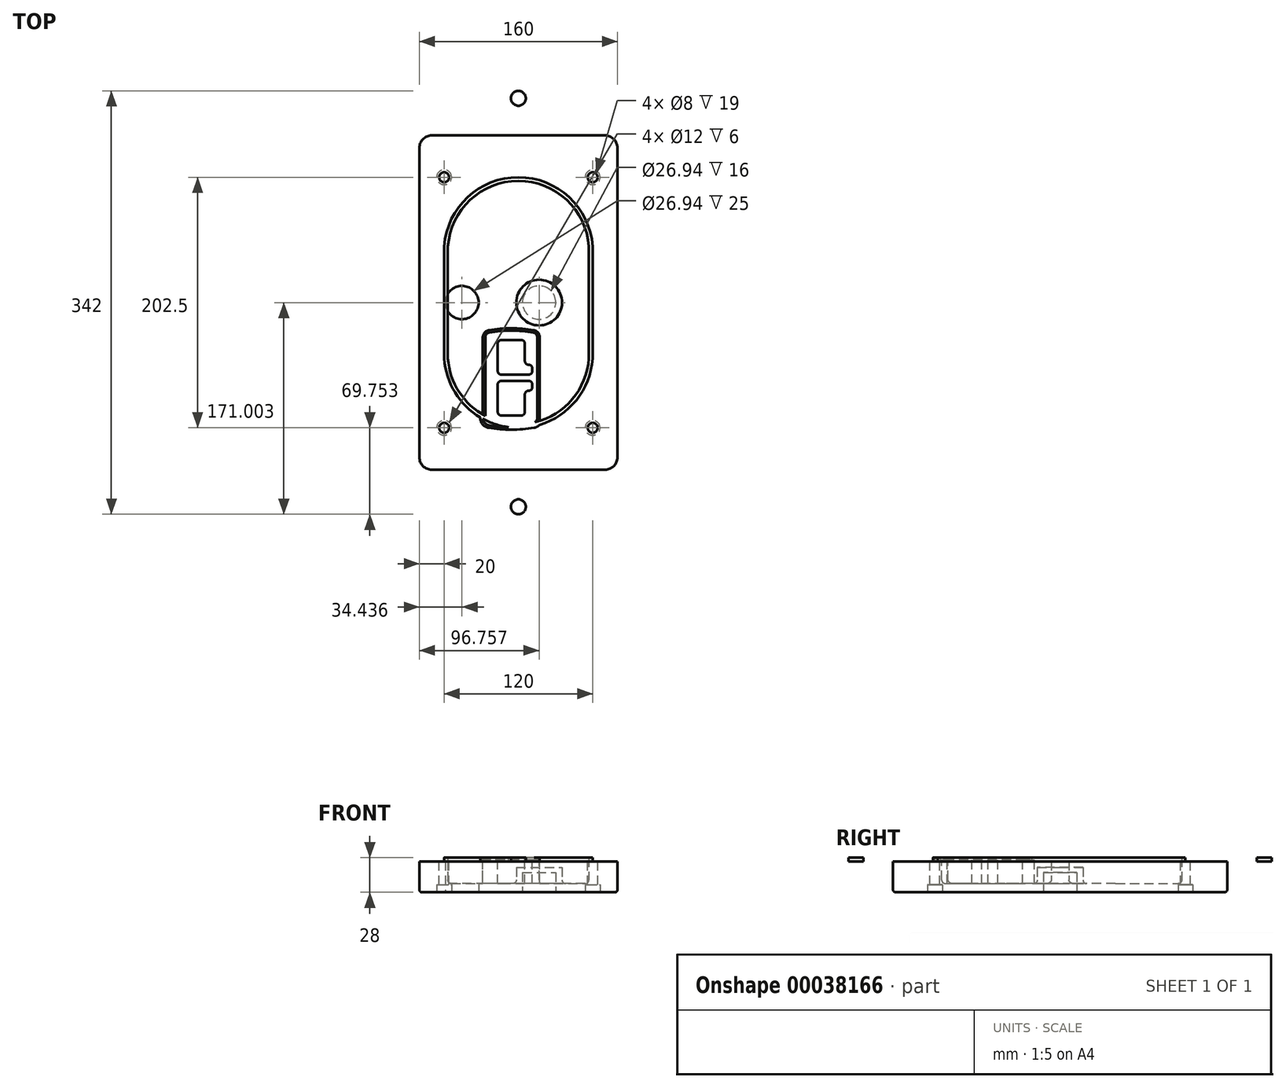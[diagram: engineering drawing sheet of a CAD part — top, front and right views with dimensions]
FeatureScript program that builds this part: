
annotation { "Feature Type Name" : "Feature", "Feature Type Description" : "" }
export const myFeature = defineFeature(function(context is Context, id is Id, definition is map)
    precondition{}
    {
        {
            var Q0;
            Q0=qCreatedBy(makeId("Top.planeOp"),FACE);
            var sketch = newSketch(context, id + "F0", { "sketchPlane" : qUnion([Q0])});
            skPoint(sketch, "E0.rect.middle", {"position": v(0, 0) * mm});
            skLineSegment(sketch, "E1.bottom", {"start": v(24.05, 28.38) * mm, "end": v(164.05, 28.38) * mm});
            skLineSegment(sketch, "E1.top", {"start": v(24.05, 298.38) * mm, "end": v(164.05, 298.38) * mm});
            skLineSegment(sketch, "E1.left", {"start": v(14.05, 38.38) * mm, "end": v(14.05, 288.38) * mm});
            skLineSegment(sketch, "E1.right", {"start": v(174.05, 38.38) * mm, "end": v(174.05, 288.38) * mm});
            skLineSegment(sketch, "E2", {"start": v(14.05, 298.38) * mm, "end": v(174.05, 28.38) * mm, "construction": true});
            skLineSegment(sketch, "E3", {"start": v(174.05, 298.38) * mm, "end": v(14.05, 28.38) * mm, "construction": true});
            skCircle(sketch, "E4", {"center": v(34.05, 264.63) * mm, "radius": 4 * mm});
            skCircle(sketch, "E5", {"center": v(154.05, 264.63) * mm, "radius": 4 * mm});
            skCircle(sketch, "E6", {"center": v(154.05, 62.13) * mm, "radius": 4 * mm});
            skCircle(sketch, "E7", {"center": v(34.05, 62.13) * mm, "radius": 4 * mm});
            skLineSegment(sketch, "E8", {"start": v(34.05, 264.63) * mm, "end": v(154.05, 264.63) * mm, "construction": true});
            skLineSegment(sketch, "E9", {"start": v(154.05, 264.63) * mm, "end": v(154.05, 62.13) * mm, "construction": true});
            skLineSegment(sketch, "E10", {"start": v(154.05, 62.13) * mm, "end": v(34.05, 62.13) * mm, "construction": true});
            skLineSegment(sketch, "E11", {"start": v(34.05, 62.13) * mm, "end": v(34.05, 264.63) * mm, "construction": true});
            skLineSegment(sketch, "E12", {"start": v(34.05, 208.05) * mm, "end": v(34.05, 118.72) * mm});
            skLineSegment(sketch, "E13", {"start": v(154.05, 208.05) * mm, "end": v(154.05, 118.72) * mm});
            skArc(sketch, "E14", {"start": v(154.03, 208.75) * mm, "mid": v(94.05, 264.63) * mm, "end": v(34.07, 208.75) * mm});
            skArc(sketch, "E15", {"start": v(34.07, 118.01) * mm, "mid": v(94.05, 62.13) * mm, "end": v(154.03, 118.01) * mm});
            skLineSegment(sketch, "E16", {"start": v(34.05, 163.38) * mm, "end": v(154.05, 163.38) * mm, "construction": true});
            skPoint(sketch, "E17.visualSharp", {"position": v(34.05, 118.38) * mm});
            skArc(sketch, "E17.filletArc", {"start": v(34.05, 118.72) * mm, "mid": v(34.06, 118.37) * mm, "end": v(34.07, 118.01) * mm});
            skPoint(sketch, "E18.visualSharp", {"position": v(34.05, 208.38) * mm});
            skArc(sketch, "E18.filletArc", {"start": v(34.07, 208.75) * mm, "mid": v(34.06, 208.4) * mm, "end": v(34.05, 208.05) * mm});
            skPoint(sketch, "E19.visualSharp", {"position": v(154.05, 208.38) * mm});
            skArc(sketch, "E19.filletArc", {"start": v(154.05, 208.05) * mm, "mid": v(154.04, 208.4) * mm, "end": v(154.03, 208.75) * mm});
            skPoint(sketch, "E20.visualSharp", {"position": v(154.05, 118.38) * mm});
            skArc(sketch, "E20.filletArc", {"start": v(154.03, 118.01) * mm, "mid": v(154.04, 118.37) * mm, "end": v(154.05, 118.72) * mm});
            skPoint(sketch, "E21.visualSharp", {"position": v(14.05, 298.38) * mm});
            skArc(sketch, "E21.filletArc", {"start": v(24.05, 298.38) * mm, "mid": v(16.98, 295.45) * mm, "end": v(14.05, 288.38) * mm});
            skPoint(sketch, "E22.visualSharp", {"position": v(174.05, 298.38) * mm});
            skArc(sketch, "E22.filletArc", {"start": v(174.05, 288.38) * mm, "mid": v(171.12, 295.45) * mm, "end": v(164.05, 298.38) * mm});
            skPoint(sketch, "E23.visualSharp", {"position": v(174.05, 28.38) * mm});
            skArc(sketch, "E23.filletArc", {"start": v(164.05, 28.38) * mm, "mid": v(171.12, 31.31) * mm, "end": v(174.05, 38.38) * mm});
            skPoint(sketch, "E24.visualSharp", {"position": v(14.05, 28.38) * mm});
            skArc(sketch, "E24.filletArc", {"start": v(14.05, 38.38) * mm, "mid": v(16.98, 31.31) * mm, "end": v(24.05, 28.38) * mm});
            skArc(sketch, "E25.0", {"start": v(151.05, 208.05) * mm, "mid": v(151.05, 208.3) * mm, "end": v(151.03, 208.54) * mm});
            skLineSegment(sketch, "E25.1", {"start": v(151.05, 208.05) * mm, "end": v(151.05, 118.72) * mm});
            skArc(sketch, "E25.2", {"start": v(151.03, 118.23) * mm, "mid": v(151.05, 118.47) * mm, "end": v(151.05, 118.72) * mm});
            skArc(sketch, "E25.3", {"start": v(37.07, 118.23) * mm, "mid": v(94.05, 65.13) * mm, "end": v(151.03, 118.23) * mm});
            skArc(sketch, "E25.4", {"start": v(37.05, 118.72) * mm, "mid": v(37.05, 118.47) * mm, "end": v(37.07, 118.23) * mm});
            skArc(sketch, "E25.5", {"start": v(151.03, 208.54) * mm, "mid": v(94.05, 261.63) * mm, "end": v(37.07, 208.54) * mm});
            skLineSegment(sketch, "E25.6", {"start": v(37.05, 208.05) * mm, "end": v(37.05, 118.72) * mm});
            skArc(sketch, "E25.7", {"start": v(37.07, 208.54) * mm, "mid": v(37.05, 208.3) * mm, "end": v(37.05, 208.05) * mm});
            skArc(sketch, "E26.0", {"start": v(30.08, 209.03) * mm, "mid": v(30.06, 208.54) * mm, "end": v(30.05, 208.05) * mm});
            skArc(sketch, "E26.1", {"start": v(158.02, 209.03) * mm, "mid": v(94.05, 268.63) * mm, "end": v(30.08, 209.03) * mm});
            skArc(sketch, "E26.2", {"start": v(158.05, 208.05) * mm, "mid": v(158.04, 208.54) * mm, "end": v(158.02, 209.03) * mm});
            skLineSegment(sketch, "E26.3", {"start": v(158.05, 208.05) * mm, "end": v(158.05, 118.72) * mm});
            skArc(sketch, "E26.4", {"start": v(158.02, 117.73) * mm, "mid": v(158.04, 118.23) * mm, "end": v(158.05, 118.72) * mm});
            skLineSegment(sketch, "E26.5", {"start": v(30.05, 208.05) * mm, "end": v(30.05, 118.72) * mm});
            skArc(sketch, "E26.6", {"start": v(30.08, 117.73) * mm, "mid": v(94.05, 58.13) * mm, "end": v(158.02, 117.73) * mm});
            skArc(sketch, "E26.7", {"start": v(30.05, 118.72) * mm, "mid": v(30.06, 118.23) * mm, "end": v(30.08, 117.73) * mm});
            skSolve(sketch);
        }
        {
            var Q0;
            Q0=makeQuery(id+"F0.imprint","IMPRINT",FACE,{"disambiguationData":[TD([[makeQuery(id+"F0.imprint","IMPRINT",EDGE,{"derivedFrom":sQuery(id+"F0.wireOp",EDGE,"E1.bottom")}),1.0]])]});
            var Q1;
            Q1=makeQuery(id+"F0.imprint","IMPRINT",FACE,{"disambiguationData":[TD([[makeQuery(id+"F0.imprint","IMPRINT",EDGE,{"derivedFrom":sQuery(id+"F0.wireOp",EDGE,"E12")}),1.0]])]});
            var Q2;
            Q2=makeQuery(id+"F0.imprint","IMPRINT",FACE,{"disambiguationData":[TD([[makeQuery(id+"F0.imprint","IMPRINT",EDGE,{"derivedFrom":sQuery(id+"F0.wireOp",EDGE,"E25.0")}),1.0]])]});
            var Q3;
            Q3=makeQuery(id+"F0.imprint","IMPRINT",FACE,{"disambiguationData":[TD([[makeQuery(id+"F0.imprint","IMPRINT",EDGE,{"derivedFrom":sQuery(id+"F0.wireOp",EDGE,"E12")}),-1.0]])]});
            extrude(context, id + "F1", {"entities" : qUnion([Q0, Q1, Q2, Q3]), "oppositeDirection" : true, "depth" : 25 * mm});
        }
        {
            var Q0;
            Q0=makeQuery(id+"F0.imprint","IMPRINT",FACE,{"disambiguationData":[TD([[makeQuery(id+"F0.imprint","IMPRINT",EDGE,{"derivedFrom":sQuery(id+"F0.wireOp",EDGE,"E12")}),1.0]])]});
            extrude(context, id + "F2", {"entities" : qUnion([Q0]), "operationType" : NewBodyOperationType.ADD, "depth" : 3 * mm});
        }
        {
            var Q0;
            Q0=makeQuery(id+"F0.imprint","IMPRINT",FACE,{"disambiguationData":[TD([[makeQuery(id+"F0.imprint","IMPRINT",EDGE,{"derivedFrom":sQuery(id+"F0.wireOp",EDGE,"E25.0")}),1.0]])]});
            extrude(context, id + "F3", {"entities" : qUnion([Q0]), "operationType" : NewBodyOperationType.REMOVE, "oppositeDirection" : true, "depth" : 18 * mm});
        }
        {
            var Q0;
            Q0=makeQuery(id+"F2.opExtrude","CAP_FACE",FACE,{"disambiguationData":[OSD([sQuery(id+"F0.wireOp",EDGE,"E12"),sQuery(id+"F0.wireOp",EDGE,"E13"),sQuery(id+"F0.wireOp",EDGE,"E14"),sQuery(id+"F0.wireOp",EDGE,"E15"),sQuery(id+"F0.wireOp",EDGE,"E17.filletArc"),sQuery(id+"F0.wireOp",EDGE,"E18.filletArc"),sQuery(id+"F0.wireOp",EDGE,"E19.filletArc"),sQuery(id+"F0.wireOp",EDGE,"E20.filletArc"),sQuery(id+"F0.wireOp",EDGE,"E25.0"),sQuery(id+"F0.wireOp",EDGE,"E25.1"),sQuery(id+"F0.wireOp",EDGE,"E25.2"),sQuery(id+"F0.wireOp",EDGE,"E25.3"),sQuery(id+"F0.wireOp",EDGE,"E25.4"),sQuery(id+"F0.wireOp",EDGE,"E25.5"),sQuery(id+"F0.wireOp",EDGE,"E25.6"),sQuery(id+"F0.wireOp",EDGE,"E25.7")])],"isStart":false});
            var sketch = newSketch(context, id + "F4", { "sketchPlane" : qUnion([Q0])});
            skArc(sketch, "E27.0", {"start": v(69.96, 62.18) * mm, "mid": v(88.3, 60.63) * mm, "end": v(106.64, 62.18) * mm});
            skArc(sketch, "E28.0", {"start": v(106.64, 143.09) * mm, "mid": v(88.3, 144.63) * mm, "end": v(69.96, 143.09) * mm});
            skLineSegment(sketch, "E29", {"start": v(63.3, 135.2) * mm, "end": v(63.3, 70.07) * mm});
            skLineSegment(sketch, "E30", {"start": v(113.3, 135.2) * mm, "end": v(113.3, 70.07) * mm});
            skLineSegment(sketch, "E31", {"start": v(63.3, 141.74) * mm, "end": v(113.3, 141.74) * mm, "construction": true});
            skLineSegment(sketch, "E32", {"start": v(63.3, 63.52) * mm, "end": v(113.3, 63.52) * mm, "construction": true});
            skPoint(sketch, "E33.visualSharp", {"position": v(63.3, 141.74) * mm});
            skArc(sketch, "E33.filletArc", {"start": v(69.96, 143.09) * mm, "mid": v(65.19, 140.36) * mm, "end": v(63.3, 135.2) * mm});
            skPoint(sketch, "E34.visualSharp", {"position": v(113.3, 141.74) * mm});
            skArc(sketch, "E34.filletArc", {"start": v(113.3, 135.2) * mm, "mid": v(111.41, 140.36) * mm, "end": v(106.64, 143.09) * mm});
            skPoint(sketch, "E35.visualSharp", {"position": v(113.3, 63.52) * mm});
            skArc(sketch, "E35.filletArc", {"start": v(106.64, 62.18) * mm, "mid": v(111.41, 64.9) * mm, "end": v(113.3, 70.07) * mm});
            skPoint(sketch, "E36.visualSharp", {"position": v(63.3, 63.52) * mm});
            skArc(sketch, "E36.filletArc", {"start": v(63.3, 70.07) * mm, "mid": v(65.19, 64.9) * mm, "end": v(69.96, 62.18) * mm});
            skArc(sketch, "E37.0", {"start": v(151.03, 208.54) * mm, "mid": v(94.05, 261.63) * mm, "end": v(37.07, 208.54) * mm});
            skArc(sketch, "E37.1", {"start": v(37.07, 208.54) * mm, "mid": v(37.05, 208.3) * mm, "end": v(37.05, 208.05) * mm});
            skLineSegment(sketch, "E37.2", {"start": v(37.05, 208.05) * mm, "end": v(37.05, 118.72) * mm});
            skArc(sketch, "E37.3", {"start": v(37.05, 118.72) * mm, "mid": v(37.05, 118.47) * mm, "end": v(37.07, 118.23) * mm});
            skArc(sketch, "E37.4", {"start": v(37.07, 118.23) * mm, "mid": v(94.05, 65.13) * mm, "end": v(151.03, 118.23) * mm});
            skArc(sketch, "E37.5", {"start": v(151.03, 118.23) * mm, "mid": v(151.05, 118.47) * mm, "end": v(151.05, 118.72) * mm});
            skLineSegment(sketch, "E37.6", {"start": v(151.05, 208.05) * mm, "end": v(151.05, 118.72) * mm});
            skArc(sketch, "E37.7", {"start": v(151.05, 208.05) * mm, "mid": v(151.05, 208.3) * mm, "end": v(151.03, 208.54) * mm});
            skLineSegment(sketch, "E38.0", {"start": v(111.3, 135.2) * mm, "end": v(111.3, 70.07) * mm});
            skArc(sketch, "E38.1", {"start": v(106.3, 64.15) * mm, "mid": v(109.88, 66.2) * mm, "end": v(111.3, 70.07) * mm});
            skArc(sketch, "E38.2", {"start": v(70.3, 64.15) * mm, "mid": v(88.3, 62.63) * mm, "end": v(106.3, 64.15) * mm});
            skArc(sketch, "E38.3", {"start": v(65.3, 70.07) * mm, "mid": v(66.72, 66.2) * mm, "end": v(70.3, 64.15) * mm});
            skLineSegment(sketch, "E38.4", {"start": v(65.3, 135.2) * mm, "end": v(65.3, 70.07) * mm});
            skArc(sketch, "E38.5", {"start": v(111.3, 135.2) * mm, "mid": v(109.88, 139.07) * mm, "end": v(106.3, 141.11) * mm});
            skArc(sketch, "E38.6", {"start": v(70.3, 141.11) * mm, "mid": v(66.72, 139.07) * mm, "end": v(65.3, 135.2) * mm});
            skArc(sketch, "E38.7", {"start": v(106.3, 141.11) * mm, "mid": v(88.3, 142.63) * mm, "end": v(70.3, 141.11) * mm});
            skArc(sketch, "E39.0", {"start": v(109.3, 135.2) * mm, "mid": v(108.36, 137.78) * mm, "end": v(105.97, 139.14) * mm});
            skLineSegment(sketch, "E39.1", {"start": v(109.3, 135.2) * mm, "end": v(109.3, 70.07) * mm});
            skArc(sketch, "E39.2", {"start": v(105.97, 66.12) * mm, "mid": v(108.36, 67.49) * mm, "end": v(109.3, 70.07) * mm});
            skArc(sketch, "E39.3", {"start": v(70.63, 66.12) * mm, "mid": v(88.3, 64.63) * mm, "end": v(105.97, 66.12) * mm});
            skArc(sketch, "E39.4", {"start": v(67.3, 70.07) * mm, "mid": v(68.24, 67.49) * mm, "end": v(70.63, 66.12) * mm});
            skArc(sketch, "E39.5", {"start": v(105.97, 139.14) * mm, "mid": v(88.3, 140.63) * mm, "end": v(70.63, 139.14) * mm});
            skLineSegment(sketch, "E39.6", {"start": v(67.3, 135.2) * mm, "end": v(67.3, 70.07) * mm});
            skArc(sketch, "E39.7", {"start": v(70.63, 139.14) * mm, "mid": v(68.24, 137.78) * mm, "end": v(67.3, 135.2) * mm});
            skLineSegment(sketch, "E40", {"start": v(63.3, 102.63) * mm, "end": v(113.3, 102.63) * mm, "construction": true});
            skLineSegment(sketch, "E41", {"start": v(77.3, 108.13) * mm, "end": v(77.3, 130.13) * mm});
            skLineSegment(sketch, "E42", {"start": v(80.3, 133.13) * mm, "end": v(96.3, 133.13) * mm});
            skLineSegment(sketch, "E43", {"start": v(99.3, 130.13) * mm, "end": v(99.3, 116.13) * mm});
            skLineSegment(sketch, "E44", {"start": v(102.3, 113.13) * mm, "end": v(102.3, 113.13) * mm});
            skLineSegment(sketch, "E45", {"start": v(105.3, 110.13) * mm, "end": v(105.3, 108.13) * mm});
            skLineSegment(sketch, "E46", {"start": v(102.3, 105.13) * mm, "end": v(80.3, 105.13) * mm});
            skPoint(sketch, "E47.visualSharp", {"position": v(77.3, 133.13) * mm});
            skArc(sketch, "E47.filletArc", {"start": v(80.3, 133.13) * mm, "mid": v(78.18, 132.25) * mm, "end": v(77.3, 130.13) * mm});
            skPoint(sketch, "E48.visualSharp", {"position": v(99.3, 133.13) * mm});
            skArc(sketch, "E48.filletArc", {"start": v(99.3, 130.13) * mm, "mid": v(98.42, 132.25) * mm, "end": v(96.3, 133.13) * mm});
            skPoint(sketch, "E49.visualSharp", {"position": v(99.3, 113.13) * mm});
            skArc(sketch, "E49.filletArc", {"start": v(99.3, 116.13) * mm, "mid": v(100.18, 114.01) * mm, "end": v(102.3, 113.13) * mm});
            skPoint(sketch, "E50.visualSharp", {"position": v(105.3, 113.13) * mm});
            skArc(sketch, "E50.filletArc", {"start": v(105.3, 110.13) * mm, "mid": v(104.42, 112.25) * mm, "end": v(102.3, 113.13) * mm});
            skPoint(sketch, "E51.visualSharp", {"position": v(105.3, 105.13) * mm});
            skArc(sketch, "E51.filletArc", {"start": v(102.3, 105.13) * mm, "mid": v(104.42, 106.01) * mm, "end": v(105.3, 108.13) * mm});
            skPoint(sketch, "E52.visualSharp", {"position": v(77.3, 105.13) * mm});
            skArc(sketch, "E52.filletArc", {"start": v(77.3, 108.13) * mm, "mid": v(78.18, 106.01) * mm, "end": v(80.3, 105.13) * mm});
            skLineSegment(sketch, "E53.0.MirrorCS", {"start": v(102.3, 100.13) * mm, "end": v(80.3, 100.13) * mm});
            skArc(sketch, "E54.0.MirrorCS", {"start": v(77.3, 97.13) * mm, "mid": v(78.18, 99.25) * mm, "end": v(80.3, 100.13) * mm});
            skLineSegment(sketch, "E55.0.MirrorCS", {"start": v(77.3, 97.13) * mm, "end": v(77.3, 75.13) * mm});
            skArc(sketch, "E56.0.MirrorCS", {"start": v(80.3, 72.13) * mm, "mid": v(78.18, 73.01) * mm, "end": v(77.3, 75.13) * mm});
            skLineSegment(sketch, "E57.0.MirrorCS", {"start": v(80.3, 72.13) * mm, "end": v(96.3, 72.13) * mm});
            skArc(sketch, "E58.0.MirrorCS", {"start": v(99.3, 75.13) * mm, "mid": v(98.42, 73.01) * mm, "end": v(96.3, 72.13) * mm});
            skLineSegment(sketch, "E59.0.MirrorCS", {"start": v(99.3, 75.13) * mm, "end": v(99.3, 89.13) * mm});
            skArc(sketch, "E60.0.MirrorCS", {"start": v(99.3, 89.13) * mm, "mid": v(100.18, 91.25) * mm, "end": v(102.3, 92.13) * mm});
            skArc(sketch, "E61.0.MirrorCS", {"start": v(105.3, 95.13) * mm, "mid": v(104.42, 93.01) * mm, "end": v(102.3, 92.13) * mm});
            skLineSegment(sketch, "E62.0.MirrorCS", {"start": v(105.3, 95.13) * mm, "end": v(105.3, 97.13) * mm});
            skArc(sketch, "E63.0.MirrorCS", {"start": v(102.3, 100.13) * mm, "mid": v(104.42, 99.25) * mm, "end": v(105.3, 97.13) * mm});
            skSolve(sketch);
        }
        {
            var Q0;
            Q0=makeQuery(id+"F4.imprint","IMPRINT",FACE,{"disambiguationData":[TD([[makeQuery(id+"F4.imprint","IMPRINT",EDGE,{"derivedFrom":sQuery(id+"F4.wireOp",EDGE,"E27.0")}),1.0]])]});
            var Q1;
            Q1=makeQuery(id+"F4.imprint","IMPRINT",FACE,{"disambiguationData":[TD([[makeQuery(id+"F4.imprint","IMPRINT",EDGE,{"derivedFrom":sQuery(id+"F4.wireOp",EDGE,"E38.0")}),-1.0]])]});
            var Q2;
            Q2=makeQuery(id+"F4.imprint","IMPRINT",FACE,{"disambiguationData":[TD([[makeQuery(id+"F4.imprint","IMPRINT",EDGE,{"derivedFrom":sQuery(id+"F4.wireOp",EDGE,"E39.0")}),1.0]])]});
            extrude(context, id + "F5", {"entities" : qUnion([Q0, Q1, Q2]), "operationType" : NewBodyOperationType.ADD, "endBound" : BoundingType.UP_TO_NEXT, "oppositeDirection" : true, "depth" : 25 * mm});
        }
        {
            var Q0;
            Q0=makeQuery(id+"F4.imprint","IMPRINT",FACE,{"disambiguationData":[TD([[makeQuery(id+"F4.imprint","IMPRINT",EDGE,{"derivedFrom":sQuery(id+"F4.wireOp",EDGE,"E38.0")}),-1.0]])]});
            extrude(context, id + "F6", {"entities" : qUnion([Q0]), "operationType" : NewBodyOperationType.REMOVE, "oppositeDirection" : true, "depth" : 2 * mm});
        }
        {
            var Q0;
            Q0=makeQuery(id+"F1.opExtrude","CAP_FACE",FACE,{"disambiguationData":[OSD([sQuery(id+"F0.wireOp",EDGE,"E1.bottom"),sQuery(id+"F0.wireOp",EDGE,"E1.top"),sQuery(id+"F0.wireOp",EDGE,"E1.left"),sQuery(id+"F0.wireOp",EDGE,"E1.right"),sQuery(id+"F0.wireOp",EDGE,"E4"),sQuery(id+"F0.wireOp",EDGE,"E5"),sQuery(id+"F0.wireOp",EDGE,"E6"),sQuery(id+"F0.wireOp",EDGE,"E7"),sQuery(id+"F0.wireOp",EDGE,"E21.filletArc"),sQuery(id+"F0.wireOp",EDGE,"E22.filletArc"),sQuery(id+"F0.wireOp",EDGE,"E23.filletArc"),sQuery(id+"F0.wireOp",EDGE,"E24.filletArc")])],"isStart":false});
            var sketch = newSketch(context, id + "F7", { "sketchPlane" : qUnion([Q0])});
            skCircle(sketch, "E64", {"center": v(110.8, -163.38) * mm, "radius": 13.47 * mm});
            skCircle(sketch, "E65", {"center": v(48.49, -163.38) * mm, "radius": 13.47 * mm});
            skLineSegment(sketch, "E66", {"start": v(174.05, -163.38) * mm, "end": v(14.05, -163.38) * mm});
            skCircle(sketch, "E67", {"center": v(110.8, -163.38) * mm, "radius": 18.47 * mm});
            skCircle(sketch, "E68", {"center": v(154.05, -264.63) * mm, "radius": 6 * mm});
            skCircle(sketch, "E69", {"center": v(34.05, -264.63) * mm, "radius": 6 * mm});
            skCircle(sketch, "E70", {"center": v(34.05, -62.13) * mm, "radius": 6 * mm});
            skCircle(sketch, "E71", {"center": v(154.05, -62.13) * mm, "radius": 6 * mm});
            skSolve(sketch);
        }
        {
            var Q0;
            {var subQ1=sQuery(id+"F7.wireOp",EDGE,"E66");var subQ4=sQuery(id+"F7.wireOp",EDGE,"E64");var subQ6=makeQuery(id+"F7.imprint","INTERSECT",VERTEX,{"disambiguationData":[OD(0.0)],"derivedFrom":[subQ4,subQ1]});Q0=makeQuery(id+"F7.imprint","IMPRINT",FACE,{"disambiguationData":[TD([[makeQuery(id+"F7.imprint","IMPRINT",EDGE,{"disambiguationData":[TD([[subQ6,-1.0]])],"derivedFrom":subQ4}),-1.0]])]});}
            var Q1;
            {var subQ0=sQuery(id+"F7.wireOp",EDGE,"E66");var subQ1=sQuery(id+"F7.wireOp",EDGE,"E64");var subQ3=makeQuery(id+"F7.imprint","INTERSECT",VERTEX,{"disambiguationData":[OD(0.0)],"derivedFrom":[subQ1,subQ0]});Q1=makeQuery(id+"F7.imprint","IMPRINT",FACE,{"disambiguationData":[TD([[makeQuery(id+"F7.imprint","IMPRINT",EDGE,{"disambiguationData":[TD([[subQ3,-1.0]])],"derivedFrom":subQ1}),1.0]])]});}
            var Q2;
            {var subQ0=sQuery(id+"F7.wireOp",EDGE,"E66");var subQ1=sQuery(id+"F7.wireOp",EDGE,"E64");var subQ3=makeQuery(id+"F7.imprint","INTERSECT",VERTEX,{"disambiguationData":[OD(0.0)],"derivedFrom":[subQ1,subQ0]});Q2=makeQuery(id+"F7.imprint","IMPRINT",FACE,{"disambiguationData":[TD([[makeQuery(id+"F7.imprint","IMPRINT",EDGE,{"disambiguationData":[TD([[subQ3,1.0]])],"derivedFrom":subQ1}),1.0]])]});}
            var Q3;
            {var subQ1=sQuery(id+"F7.wireOp",EDGE,"E66");var subQ4=sQuery(id+"F7.wireOp",EDGE,"E64");var subQ6=makeQuery(id+"F7.imprint","INTERSECT",VERTEX,{"disambiguationData":[OD(0.0)],"derivedFrom":[subQ4,subQ1]});Q3=makeQuery(id+"F7.imprint","IMPRINT",FACE,{"disambiguationData":[TD([[makeQuery(id+"F7.imprint","IMPRINT",EDGE,{"disambiguationData":[TD([[subQ6,1.0]])],"derivedFrom":subQ4}),-1.0]])]});}
            extrude(context, id + "F8", {"entities" : qUnion([Q0, Q1, Q2, Q3]), "operationType" : NewBodyOperationType.ADD, "oppositeDirection" : true, "depth" : 20 * mm});
        }
        {
            var Q0;
            {var subQ0=sQuery(id+"F7.wireOp",EDGE,"E66");var subQ1=sQuery(id+"F7.wireOp",EDGE,"E64");var subQ3=makeQuery(id+"F7.imprint","INTERSECT",VERTEX,{"disambiguationData":[OD(0.0)],"derivedFrom":[subQ1,subQ0]});Q0=makeQuery(id+"F7.imprint","IMPRINT",FACE,{"disambiguationData":[TD([[makeQuery(id+"F7.imprint","IMPRINT",EDGE,{"disambiguationData":[TD([[subQ3,-1.0]])],"derivedFrom":subQ1}),1.0]])]});}
            var Q1;
            {var subQ0=sQuery(id+"F7.wireOp",EDGE,"E66");var subQ1=sQuery(id+"F7.wireOp",EDGE,"E64");var subQ3=makeQuery(id+"F7.imprint","INTERSECT",VERTEX,{"disambiguationData":[OD(0.0)],"derivedFrom":[subQ1,subQ0]});Q1=makeQuery(id+"F7.imprint","IMPRINT",FACE,{"disambiguationData":[TD([[makeQuery(id+"F7.imprint","IMPRINT",EDGE,{"disambiguationData":[TD([[subQ3,1.0]])],"derivedFrom":subQ1}),1.0]])]});}
            extrude(context, id + "F9", {"entities" : qUnion([Q0, Q1]), "operationType" : NewBodyOperationType.REMOVE, "oppositeDirection" : true, "depth" : 16 * mm});
        }
        {
            var Q0;
            {var subQ0=sQuery(id+"F7.wireOp",EDGE,"E66");var subQ1=sQuery(id+"F7.wireOp",EDGE,"E65");var subQ3=makeQuery(id+"F7.imprint","INTERSECT",VERTEX,{"disambiguationData":[OD(0.0)],"derivedFrom":[subQ1,subQ0]});Q0=makeQuery(id+"F7.imprint","IMPRINT",FACE,{"disambiguationData":[TD([[makeQuery(id+"F7.imprint","IMPRINT",EDGE,{"disambiguationData":[TD([[subQ3,-1.0]])],"derivedFrom":subQ1}),1.0]])]});}
            var Q1;
            {var subQ0=sQuery(id+"F7.wireOp",EDGE,"E66");var subQ1=sQuery(id+"F7.wireOp",EDGE,"E65");var subQ3=makeQuery(id+"F7.imprint","INTERSECT",VERTEX,{"disambiguationData":[OD(0.0)],"derivedFrom":[subQ1,subQ0]});Q1=makeQuery(id+"F7.imprint","IMPRINT",FACE,{"disambiguationData":[TD([[makeQuery(id+"F7.imprint","IMPRINT",EDGE,{"disambiguationData":[TD([[subQ3,1.0]])],"derivedFrom":subQ1}),1.0]])]});}
            extrude(context, id + "F10", {"entities" : qUnion([Q0, Q1]), "operationType" : NewBodyOperationType.REMOVE, "oppositeDirection" : true, "depth" : 25 * mm});
        }
        {
            var Q0;
            Q0=makeQuery(id+"F7.imprint","IMPRINT",FACE,{"disambiguationData":[TD([[makeQuery(id+"F7.imprint","IMPRINT",EDGE,{"derivedFrom":sQuery(id+"F7.wireOp",EDGE,"E68")}),1.0]])]});
            var Q1;
            Q1=makeQuery(id+"F7.imprint","IMPRINT",FACE,{"disambiguationData":[TD([[makeQuery(id+"F7.imprint","IMPRINT",EDGE,{"derivedFrom":makeQuery(id+"F1.opExtrude","CAP_EDGE",EDGE,{"disambiguationData":[OSD([sQuery(id+"F0.wireOp",EDGE,"E5")])],"isStart":false})}),-1.0]])]});
            var Q2;
            Q2=makeQuery(id+"F7.imprint","IMPRINT",FACE,{"disambiguationData":[TD([[makeQuery(id+"F7.imprint","IMPRINT",EDGE,{"derivedFrom":sQuery(id+"F7.wireOp",EDGE,"E69")}),1.0]])]});
            var Q3;
            Q3=makeQuery(id+"F7.imprint","IMPRINT",FACE,{"disambiguationData":[TD([[makeQuery(id+"F7.imprint","IMPRINT",EDGE,{"derivedFrom":makeQuery(id+"F1.opExtrude","CAP_EDGE",EDGE,{"disambiguationData":[OSD([sQuery(id+"F0.wireOp",EDGE,"E4")])],"isStart":false})}),-1.0]])]});
            var Q4;
            Q4=makeQuery(id+"F7.imprint","IMPRINT",FACE,{"disambiguationData":[TD([[makeQuery(id+"F7.imprint","IMPRINT",EDGE,{"derivedFrom":sQuery(id+"F7.wireOp",EDGE,"E70")}),1.0]])]});
            var Q5;
            Q5=makeQuery(id+"F7.imprint","IMPRINT",FACE,{"disambiguationData":[TD([[makeQuery(id+"F7.imprint","IMPRINT",EDGE,{"derivedFrom":makeQuery(id+"F1.opExtrude","CAP_EDGE",EDGE,{"disambiguationData":[OSD([sQuery(id+"F0.wireOp",EDGE,"E7")])],"isStart":false})}),-1.0]])]});
            var Q6;
            Q6=makeQuery(id+"F7.imprint","IMPRINT",FACE,{"disambiguationData":[TD([[makeQuery(id+"F7.imprint","IMPRINT",EDGE,{"derivedFrom":sQuery(id+"F7.wireOp",EDGE,"E71")}),1.0]])]});
            var Q7;
            Q7=makeQuery(id+"F7.imprint","IMPRINT",FACE,{"disambiguationData":[TD([[makeQuery(id+"F7.imprint","IMPRINT",EDGE,{"derivedFrom":makeQuery(id+"F1.opExtrude","CAP_EDGE",EDGE,{"disambiguationData":[OSD([sQuery(id+"F0.wireOp",EDGE,"E6")])],"isStart":false})}),-1.0]])]});
            extrude(context, id + "F11", {"entities" : qUnion([Q0, Q1, Q2, Q3, Q4, Q5, Q6, Q7]), "operationType" : NewBodyOperationType.REMOVE, "oppositeDirection" : true, "depth" : 6 * mm});
        }
        {
            var Q0;
            Q0=makeQuery(id+"F9.boolean.opBoolean","COPY",FACE,{"derivedFrom":makeQuery(id+"F9.opExtrude","CAP_FACE",FACE,{"disambiguationData":[OSD([sQuery(id+"F7.wireOp",EDGE,"E64")])],"isStart":false})});
            var sketch = newSketch(context, id + "F12", { "sketchPlane" : qUnion([Q0])});
            skArc(sketch, "E72.0", {"start": v(99.3, -148.94) * mm, "mid": v(119.29, -179.79) * mm, "end": v(105.67, -145.64) * mm});
            skArc(sketch, "E72.1", {"start": v(105.27, -145.76) * mm, "mid": v(102.14, -147.07) * mm, "end": v(99.3, -148.94) * mm});
            skLineSegment(sketch, "E73", {"start": v(92.5, -105.13) * mm, "end": v(102.3, -105.13) * mm});
            skLineSegment(sketch, "E74.0", {"start": v(102.3, -100.13) * mm, "end": v(92.5, -100.13) * mm});
            skArc(sketch, "E74.1", {"start": v(102.3, -100.13) * mm, "mid": v(104.42, -99.25) * mm, "end": v(105.3, -97.13) * mm});
            skLineSegment(sketch, "E74.2", {"start": v(105.3, -95.13) * mm, "end": v(105.3, -97.13) * mm});
            skArc(sketch, "E74.3", {"start": v(105.3, -95.13) * mm, "mid": v(104.42, -93.01) * mm, "end": v(102.3, -92.13) * mm});
            skArc(sketch, "E74.4", {"start": v(99.3, -89.13) * mm, "mid": v(100.18, -91.25) * mm, "end": v(102.3, -92.13) * mm});
            skLineSegment(sketch, "E74.5", {"start": v(99.3, -89.13) * mm, "end": v(99.3, -148.94) * mm});
            skLineSegment(sketch, "E74.7", {"start": v(102.3, -105.13) * mm, "end": v(92.5, -105.13) * mm});
            skArc(sketch, "E74.8", {"start": v(102.3, -105.13) * mm, "mid": v(104.42, -106.01) * mm, "end": v(105.3, -108.13) * mm});
            skLineSegment(sketch, "E74.9", {"start": v(105.3, -110.13) * mm, "end": v(105.3, -108.13) * mm});
            skArc(sketch, "E74.10", {"start": v(105.3, -110.13) * mm, "mid": v(104.42, -112.25) * mm, "end": v(102.3, -113.13) * mm});
            skArc(sketch, "E74.11", {"start": v(99.3, -116.13) * mm, "mid": v(100.18, -114.01) * mm, "end": v(102.3, -113.13) * mm});
            skLineSegment(sketch, "E74.12", {"start": v(99.3, -148.94) * mm, "end": v(99.3, -116.13) * mm});
            skPoint(sketch, "E75.orphan", {"position": v(99.3, -130.13) * mm});
            skPoint(sketch, "E76.orphan", {"position": v(80.3, -105.13) * mm});
            skPoint(sketch, "E77.orphan", {"position": v(80.3, -100.13) * mm});
            skPoint(sketch, "E78.orphan", {"position": v(99.3, -75.13) * mm});
            skSolve(sketch);
        }
        {
            var Q0;
            {var subQ7=sQuery(id+"F12.wireOp",EDGE,"E72.0");var subQ14=sQuery(id+"F12.wireOp",EDGE,"E72.1");var subQ16=sQuery(id+"F12.wireOp",EDGE,"E74.1");var subQ18=sQuery(id+"F12.wireOp",EDGE,"E74.8");Q0=qUnion([makeQuery(id+"F12.imprint","IMPRINT",FACE,{"disambiguationData":[TD([[makeQuery(id+"F12.imprint","IMPRINT",EDGE,{"derivedFrom":subQ7}),1.0]])]}),makeQuery(id+"F12.imprint","IMPRINT",FACE,{"disambiguationData":[TD([[makeQuery(id+"F12.imprint","IMPRINT",EDGE,{"derivedFrom":subQ14}),1.0]])]}),makeQuery(id+"F12.imprint","IMPRINT",FACE,{"disambiguationData":[TD([[makeQuery(id+"F12.imprint","IMPRINT",EDGE,{"derivedFrom":subQ16}),1.0]])]}),makeQuery(id+"F12.imprint","IMPRINT",FACE,{"disambiguationData":[TD([[makeQuery(id+"F12.imprint","IMPRINT",EDGE,{"derivedFrom":subQ18}),-1.0]])]})]);}
            var Q1;
            Q1=makeQuery(id+"F5.boolean.opBoolean","SPLIT",FACE,{"disambiguationData":[TD([makeQuery(id+"F5.opExtrude","SWEPT_FACE",FACE,{"disambiguationData":[OSD([sQuery(id+"F4.wireOp",EDGE,"E41")])]})])],"derivedFrom":makeQuery(id+"F3.boolean.opBoolean","COPY",FACE,{"derivedFrom":makeQuery(id+"F3.opExtrude","CAP_FACE",FACE,{"disambiguationData":[OSD([sQuery(id+"F0.wireOp",EDGE,"E25.0"),sQuery(id+"F0.wireOp",EDGE,"E25.1"),sQuery(id+"F0.wireOp",EDGE,"E25.2"),sQuery(id+"F0.wireOp",EDGE,"E25.3"),sQuery(id+"F0.wireOp",EDGE,"E25.4"),sQuery(id+"F0.wireOp",EDGE,"E25.5"),sQuery(id+"F0.wireOp",EDGE,"E25.6"),sQuery(id+"F0.wireOp",EDGE,"E25.7")])],"isStart":false})})});
            extrude(context, id + "F13", {"entities" : qUnion([Q0]), "operationType" : NewBodyOperationType.REMOVE, "endBound" : BoundingType.UP_TO_SURFACE, "endBoundEntityFace" : qUnion([Q1]), "depth" : 25 * mm});
        }
        {
            var Q0;
            Q0=makeQuery(id+"F3.boolean.opBoolean","COPY",EDGE,{"derivedFrom":makeQuery(id+"F3.opExtrude","CAP_EDGE",EDGE,{"disambiguationData":[OSD([sQuery(id+"F0.wireOp",EDGE,"E25.6")])],"isStart":false})});
            var Q1;
            Q1=makeQuery(id+"F8.boolean.opBoolean","INTERSECT",EDGE,{"derivedFrom":[makeQuery(id+"F5.opExtrude","SWEPT_FACE",FACE,{"disambiguationData":[OSD([sQuery(id+"F4.wireOp",EDGE,"E30")])]}),makeQuery(id+"F8.opExtrude","CAP_FACE",FACE,{"disambiguationData":[OSD([sQuery(id+"F7.wireOp",EDGE,"E67")])],"isStart":false})]});
            var Q2;
            Q2=makeQuery(id+"F8.boolean.opBoolean","INTERSECT",EDGE,{"disambiguationData":[OD(1.0)],"derivedFrom":[makeQuery(id+"F5.opExtrude","SWEPT_FACE",FACE,{"disambiguationData":[OSD([sQuery(id+"F4.wireOp",EDGE,"E30")])]}),makeQuery(id+"F8.opExtrude","SWEPT_FACE",FACE,{"disambiguationData":[OSD([sQuery(id+"F7.wireOp",EDGE,"E67")])]})]});
            var Q3;
            {var subQ0=makeQuery(id+"F3.boolean.opBoolean","COPY",FACE,{"derivedFrom":makeQuery(id+"F3.opExtrude","CAP_FACE",FACE,{"disambiguationData":[OSD([sQuery(id+"F0.wireOp",EDGE,"E25.0"),sQuery(id+"F0.wireOp",EDGE,"E25.1"),sQuery(id+"F0.wireOp",EDGE,"E25.2"),sQuery(id+"F0.wireOp",EDGE,"E25.3"),sQuery(id+"F0.wireOp",EDGE,"E25.4"),sQuery(id+"F0.wireOp",EDGE,"E25.5"),sQuery(id+"F0.wireOp",EDGE,"E25.6"),sQuery(id+"F0.wireOp",EDGE,"E25.7")])],"isStart":false})});var subQ1=sQuery(id+"F4.wireOp",EDGE,"E30");Q3=makeQuery(id+"F8.boolean.opBoolean","SPLIT",EDGE,{"disambiguationData":[TD([makeQuery(id+"F5.opExtrude","SWEPT_FACE",FACE,{"disambiguationData":[OSD([sQuery(id+"F4.wireOp",EDGE,"E35.filletArc")])]})])],"derivedFrom":makeQuery(id+"F5.opExtrude","TWEAK_EDGE",EDGE,{"derivedFrom":[subQ0,makeQuery(id+"F4.imprint","IMPRINT",EDGE,{"derivedFrom":subQ1})]})});}
            var Q4;
            {var subQ0=sQuery(id+"F0.wireOp",EDGE,"E25.0");var subQ1=sQuery(id+"F0.wireOp",EDGE,"E25.1");var subQ2=sQuery(id+"F0.wireOp",EDGE,"E25.2");var subQ3=sQuery(id+"F0.wireOp",EDGE,"E25.3");var subQ4=sQuery(id+"F0.wireOp",EDGE,"E25.4");var subQ5=sQuery(id+"F0.wireOp",EDGE,"E25.5");var subQ6=sQuery(id+"F0.wireOp",EDGE,"E25.6");var subQ7=sQuery(id+"F0.wireOp",EDGE,"E25.7");Q4=makeQuery(id+"F8.boolean.opBoolean","INTERSECT",EDGE,{"derivedFrom":[makeQuery(id+"F5.boolean.opBoolean","SPLIT",FACE,{"disambiguationData":[TD([makeQuery(id+"F2.opExtrude","SWEPT_FACE",FACE,{"disambiguationData":[OSD([subQ0])]})])],"derivedFrom":makeQuery(id+"F3.boolean.opBoolean","COPY",FACE,{"derivedFrom":makeQuery(id+"F3.opExtrude","CAP_FACE",FACE,{"disambiguationData":[OSD([subQ0,subQ1,subQ2,subQ3,subQ4,subQ5,subQ6,subQ7])],"isStart":false})})}),makeQuery(id+"F8.opExtrude","SWEPT_FACE",FACE,{"disambiguationData":[OSD([sQuery(id+"F7.wireOp",EDGE,"E67")])]})]});}
            var Q5;
            Q5=makeQuery(id+"F8.boolean.opBoolean","INTERSECT",EDGE,{"disambiguationData":[OD(0.0)],"derivedFrom":[makeQuery(id+"F5.opExtrude","SWEPT_FACE",FACE,{"disambiguationData":[OSD([sQuery(id+"F4.wireOp",EDGE,"E30")])]}),makeQuery(id+"F8.opExtrude","SWEPT_FACE",FACE,{"disambiguationData":[OSD([sQuery(id+"F7.wireOp",EDGE,"E67")])]})]});
            fillet(context, id + "F14", {"entities" : qUnion([Q0, Q1, Q2, Q3, Q4, Q5]), "radius" : 3 * mm, "tangentPropagation" : true, "allowEdgeOverflow" : false});
        }
        {
            var Q0;
            Q0=makeQuery(id+"F1.opExtrude","CAP_EDGE",EDGE,{"disambiguationData":[OSD([sQuery(id+"F0.wireOp",EDGE,"E1.bottom")])],"isStart":false});
            fillet(context, id + "F15", {"entities" : qUnion([Q0]), "radius" : 2 * mm, "tangentPropagation" : true, "allowEdgeOverflow" : false});
        }
        {
            var Q0;
            {var subQ0=sQuery(id+"F0.wireOp",EDGE,"E1.bottom");var subQ1=sQuery(id+"F0.wireOp",EDGE,"E1.top");var subQ2=sQuery(id+"F0.wireOp",EDGE,"E1.left");var subQ3=sQuery(id+"F0.wireOp",EDGE,"E1.right");var subQ4=sQuery(id+"F0.wireOp",EDGE,"E4");var subQ5=sQuery(id+"F0.wireOp",EDGE,"E5");var subQ6=sQuery(id+"F0.wireOp",EDGE,"E6");var subQ7=sQuery(id+"F0.wireOp",EDGE,"E7");var subQ8=sQuery(id+"F0.wireOp",EDGE,"E21.filletArc");var subQ9=sQuery(id+"F0.wireOp",EDGE,"E22.filletArc");var subQ10=sQuery(id+"F0.wireOp",EDGE,"E23.filletArc");var subQ11=sQuery(id+"F0.wireOp",EDGE,"E24.filletArc");Q0=makeQuery(id+"F2.boolean.opBoolean","SPLIT",FACE,{"disambiguationData":[TD([makeQuery(id+"F1.opExtrude","SWEPT_FACE",FACE,{"disambiguationData":[OSD([subQ0])]})])],"derivedFrom":makeQuery(id+"F1.opExtrude","CAP_FACE",FACE,{"disambiguationData":[OSD([subQ0,subQ1,subQ2,subQ3,subQ4,subQ5,subQ6,subQ7,subQ8,subQ9,subQ10,subQ11])],"isStart":true})});}
            var sketch = newSketch(context, id + "F16", { "sketchPlane" : qUnion([Q0])});
            skPoint(sketch, "E79.centerSnap0", {"position": v(94.05, 298.38) * mm});
            skLineSegment(sketch, "E80", {"start": v(94.05, 298.38) * mm, "end": v(94.05, 328.38) * mm, "construction": true});
            skCircle(sketch, "E81", {"center": v(94.05, 328.38) * mm, "radius": 6 * mm});
            skLineSegment(sketch, "E82", {"start": v(109.05, 316.38) * mm, "end": v(109.05, 328.38) * mm});
            skLineSegment(sketch, "E83", {"start": v(79.05, 316.38) * mm, "end": v(79.05, 328.38) * mm});
            skArc(sketch, "E84", {"start": v(109.05, 328.38) * mm, "mid": v(94.05, 343.38) * mm, "end": v(79.05, 328.38) * mm});
            skLineSegment(sketch, "E85", {"start": v(79.05, 316.38) * mm, "end": v(61.05, 298.38) * mm});
            skLineSegment(sketch, "E86", {"start": v(109.05, 316.38) * mm, "end": v(127.05, 298.38) * mm});
            skLineSegment(sketch, "E87", {"start": v(-27.12, 163.38) * mm, "end": v(202.43, 163.38) * mm, "construction": true});
            skLineSegment(sketch, "E88.MirrorCS", {"start": v(79.05, 10.38) * mm, "end": v(79.05, -1.62) * mm});
            skPoint(sketch, "E89.MirrorP", {"position": v(94.05, 28.38) * mm});
            skCircle(sketch, "E90.MirrorC", {"center": v(94.05, -1.62) * mm, "radius": 6 * mm});
            skLineSegment(sketch, "E91.MirrorCS", {"start": v(109.05, 10.38) * mm, "end": v(109.05, -1.62) * mm});
            skLineSegment(sketch, "E92.MirrorCS", {"start": v(94.05, 28.38) * mm, "end": v(94.05, -1.62) * mm});
            skArc(sketch, "E93.MirrorCS", {"start": v(109.05, -1.62) * mm, "mid": v(94.05, -16.62) * mm, "end": v(79.05, -1.62) * mm});
            skLineSegment(sketch, "E94.MirrorCS", {"start": v(79.05, 10.38) * mm, "end": v(61.05, 28.38) * mm});
            skLineSegment(sketch, "E95.MirrorCS", {"start": v(109.05, 10.38) * mm, "end": v(127.05, 28.38) * mm});
            skSolve(sketch);
        }
        {
            var Q0;
            Q0 = qSketchRegion(id + "F16", true);
            var Q1;
            Q1=makeQuery(id+"F16.imprint","IMPRINT",FACE,{"disambiguationData":[TD([[makeQuery(id+"F16.imprint","IMPRINT",EDGE,{"derivedFrom":sQuery(id+"F16.wireOp",EDGE,"E88.MirrorCS")}),1.0]])]});
            var Q2;
            Q2=makeQuery(id+"F16.imprint","IMPRINT",FACE,{"disambiguationData":[TD([[makeQuery(id+"F16.imprint","IMPRINT",EDGE,{"derivedFrom":sQuery(id+"F16.wireOp",EDGE,"E81")}),-1.0]])]});
            var Q3;
            Q3=makeQuery(id+"F16.imprint","IMPRINT",FACE,{"disambiguationData":[TD([[makeQuery(id+"F16.imprint","IMPRINT",EDGE,{"derivedFrom":makeQuery(id+"F1.opExtrude","CAP_EDGE",EDGE,{"disambiguationData":[OSD([sQuery(id+"F0.wireOp",EDGE,"E1.left")])],"isStart":true})}),-1.0]])]});
            var Q4;
            {var subQ0=sQuery(id+"F4.wireOp",EDGE,"E41");var subQ1=sQuery(id+"F4.wireOp",EDGE,"E42");var subQ2=sQuery(id+"F4.wireOp",EDGE,"E43");var subQ3=sQuery(id+"F4.wireOp",EDGE,"E45");var subQ4=sQuery(id+"F4.wireOp",EDGE,"E46");var subQ5=sQuery(id+"F4.wireOp",EDGE,"E47.filletArc");var subQ6=sQuery(id+"F4.wireOp",EDGE,"E48.filletArc");var subQ7=sQuery(id+"F4.wireOp",EDGE,"E49.filletArc");var subQ8=sQuery(id+"F4.wireOp",EDGE,"E50.filletArc");var subQ9=sQuery(id+"F4.wireOp",EDGE,"E51.filletArc");var subQ10=sQuery(id+"F4.wireOp",EDGE,"E52.filletArc");var subQ11=sQuery(id+"F4.wireOp",EDGE,"E53.0.MirrorCS");var subQ12=sQuery(id+"F4.wireOp",EDGE,"E54.0.MirrorCS");var subQ13=sQuery(id+"F4.wireOp",EDGE,"E55.0.MirrorCS");var subQ14=sQuery(id+"F4.wireOp",EDGE,"E56.0.MirrorCS");var subQ15=sQuery(id+"F4.wireOp",EDGE,"E57.0.MirrorCS");var subQ16=sQuery(id+"F4.wireOp",EDGE,"E58.0.MirrorCS");var subQ17=sQuery(id+"F4.wireOp",EDGE,"E59.0.MirrorCS");var subQ18=sQuery(id+"F4.wireOp",EDGE,"E60.0.MirrorCS");var subQ19=sQuery(id+"F4.wireOp",EDGE,"E61.0.MirrorCS");var subQ20=sQuery(id+"F4.wireOp",EDGE,"E62.0.MirrorCS");var subQ21=sQuery(id+"F4.wireOp",EDGE,"E63.0.MirrorCS");Q4=makeQuery(id+"F6.boolean.opBoolean","SPLIT",FACE,{"disambiguationData":[TD([makeQuery(id+"F5.opExtrude","SWEPT_FACE",FACE,{"disambiguationData":[OSD([subQ0])]})])],"derivedFrom":makeQuery(id+"F5.opExtrude","CAP_FACE",FACE,{"disambiguationData":[OSD([sQuery(id+"F4.wireOp",EDGE,"E27.0"),sQuery(id+"F4.wireOp",EDGE,"E28.0"),sQuery(id+"F4.wireOp",EDGE,"E29"),sQuery(id+"F4.wireOp",EDGE,"E30"),sQuery(id+"F4.wireOp",EDGE,"E33.filletArc"),sQuery(id+"F4.wireOp",EDGE,"E34.filletArc"),sQuery(id+"F4.wireOp",EDGE,"E35.filletArc"),sQuery(id+"F4.wireOp",EDGE,"E36.filletArc"),subQ0,subQ1,subQ2,subQ3,subQ4,subQ5,subQ6,subQ7,subQ8,subQ9,subQ10,subQ11,subQ12,subQ13,subQ14,subQ15,subQ16,subQ17,subQ18,subQ19,subQ20,subQ21])],"isStart":true})});}
            extrude(context, id + "F17", {"entities" : qUnion([Q0, Q1, Q2, Q3]), "endBound" : BoundingType.UP_TO_SURFACE, "endBoundEntityFace" : qUnion([Q4]), "depth" : 25 * mm});
        }
    });
